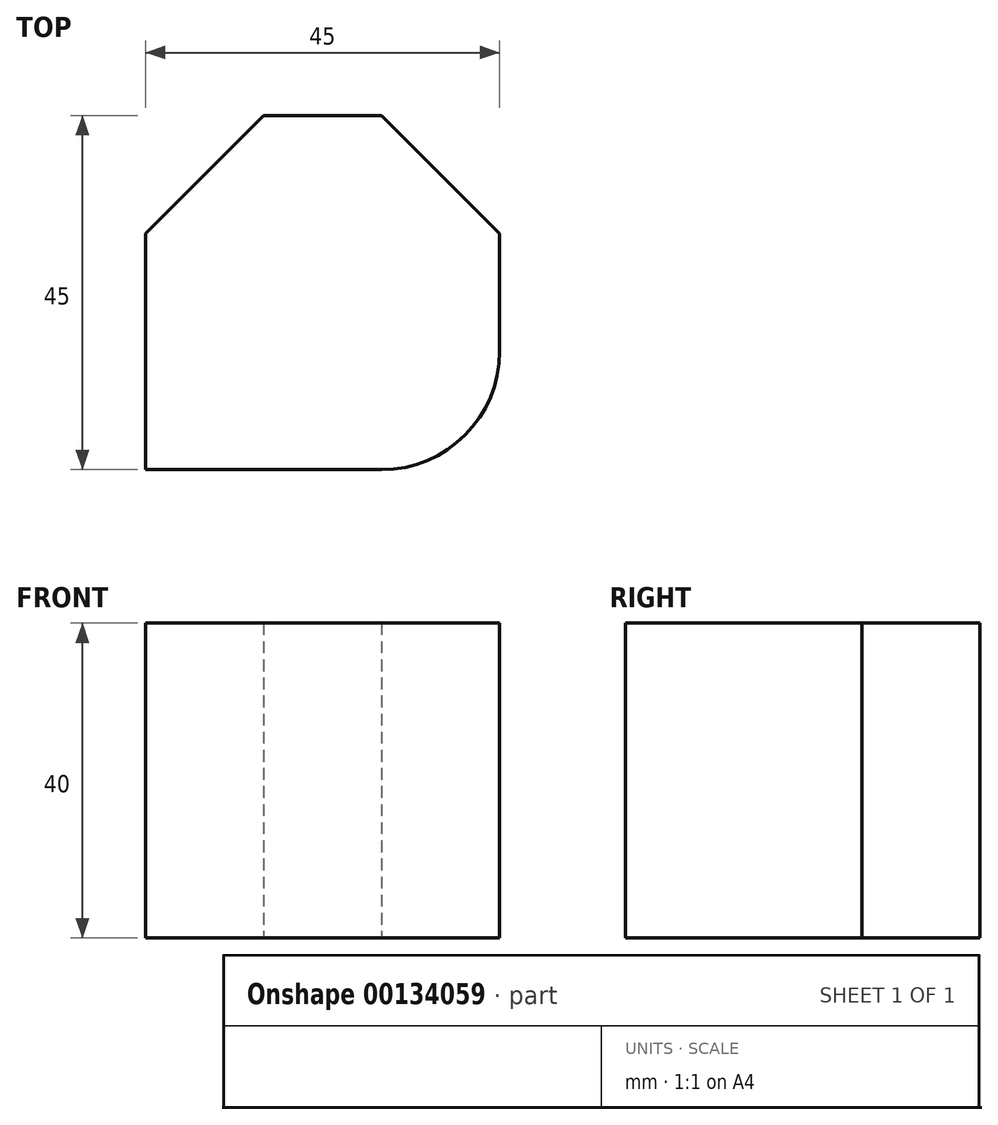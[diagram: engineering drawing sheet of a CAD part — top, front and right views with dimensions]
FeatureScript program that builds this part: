
annotation { "Feature Type Name" : "Feature", "Feature Type Description" : "" }
export const myFeature = defineFeature(function(context is Context, id is Id, definition is map)
    precondition{}
    {
        {
            var Q0;
            Q0=qCreatedBy(makeId("Top.planeOp"),FACE);
            var sketch = newSketch(context, id + "F0", { "sketchPlane" : qUnion([Q0])});
            skLineSegment(sketch, "E0", {"start": v(0, 0) * mm, "end": v(0, 30) * mm});
            skLineSegment(sketch, "E1", {"start": v(0, 30) * mm, "end": v(15, 45) * mm});
            skLineSegment(sketch, "E2", {"start": v(30, 0) * mm, "end": v(0, 0) * mm});
            skLineSegment(sketch, "E3", {"start": v(15, 45) * mm, "end": v(30, 45) * mm});
            skLineSegment(sketch, "E4", {"start": v(30, 45) * mm, "end": v(45, 30) * mm});
            skLineSegment(sketch, "E5", {"start": v(45, 30) * mm, "end": v(45, 15) * mm});
            skArc(sketch, "E6", {"start": v(30, 0) * mm, "mid": v(40.6, 4.4) * mm, "end": v(45, 15) * mm});
            skSolve(sketch);
        }
        {
            var Q0;
            Q0 = qSketchRegion(id + "F0", true);
            extrude(context, id + "F1", {"entities" : qUnion([Q0]), "depth" : 40 * mm});
        }
    });
